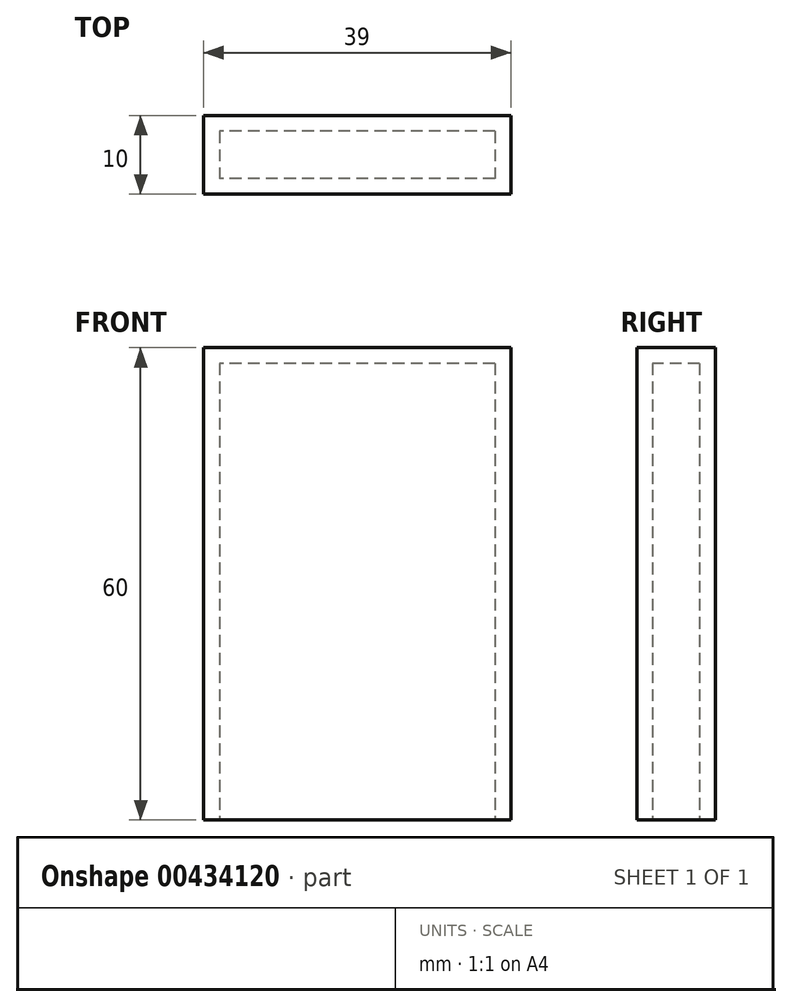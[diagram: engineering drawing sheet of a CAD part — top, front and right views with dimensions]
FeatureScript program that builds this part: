
annotation { "Feature Type Name" : "Feature", "Feature Type Description" : "" }
export const myFeature = defineFeature(function(context is Context, id is Id, definition is map)
    precondition{}
    {
        {
            var Q0;
            Q0=qCreatedBy(makeId("Top.planeOp"),FACE);
            var sketch = newSketch(context, id + "F0", { "sketchPlane" : qUnion([Q0])});
            skLineSegment(sketch, "E0.bottom", {"start": v(17.5, 3) * mm, "end": v(-17.5, 3) * mm});
            skLineSegment(sketch, "E0.top", {"start": v(17.5, -3) * mm, "end": v(-17.5, -3) * mm});
            skLineSegment(sketch, "E0.left", {"start": v(17.5, 3) * mm, "end": v(17.5, -3) * mm});
            skLineSegment(sketch, "E0.right", {"start": v(-17.5, 3) * mm, "end": v(-17.5, -3) * mm});
            skPoint(sketch, "E0.middle", {"position": v(0, 0) * mm});
            skLineSegment(sketch, "E1.0", {"start": v(19.5, 5) * mm, "end": v(-19.5, 5) * mm});
            skLineSegment(sketch, "E1.1", {"start": v(19.5, 5) * mm, "end": v(19.5, -5) * mm});
            skLineSegment(sketch, "E1.2", {"start": v(19.5, -5) * mm, "end": v(-19.5, -5) * mm});
            skLineSegment(sketch, "E1.3", {"start": v(-19.5, 5) * mm, "end": v(-19.5, -5) * mm});
            skSolve(sketch);
        }
        {
            var Q0;
            Q0 = qSketchRegion(id + "F0", true);
            extrude(context, id + "F1", {"entities" : qUnion([Q0]), "depth" : 60 * mm});
        }
        {
            var Q0;
            Q0=makeQuery(id+"F1.opExtrude","SWEPT_FACE",FACE,{"disambiguationData":[OSD([sQuery(id+"F0.wireOp",EDGE,"E1.1")])]});
            var sketch = newSketch(context, id + "F2", { "sketchPlane" : qUnion([Q0])});
            skLineSegment(sketch, "E2.bottom", {"start": v(5, 60) * mm, "end": v(-5, 60) * mm});
            skLineSegment(sketch, "E2.top", {"start": v(5, 58) * mm, "end": v(-5, 58) * mm});
            skLineSegment(sketch, "E2.left", {"start": v(5, 60) * mm, "end": v(5, 58) * mm});
            skLineSegment(sketch, "E2.right", {"start": v(-5, 60) * mm, "end": v(-5, 58) * mm});
            skSolve(sketch);
        }
        {
            var Q0;
            Q0 = qSketchRegion(id + "F2", true);
            var Q1;
            Q1=makeQuery(id+"F1.opExtrude","SWEPT_FACE",FACE,{"disambiguationData":[OSD([sQuery(id+"F0.wireOp",EDGE,"E1.3")])]});
            extrude(context, id + "F3", {"entities" : qUnion([Q0]), "operationType" : NewBodyOperationType.ADD, "endBound" : BoundingType.UP_TO_SURFACE, "oppositeDirection" : true, "endBoundEntityFace" : qUnion([Q1]), "depth" : 25 * mm});
        }
    });
